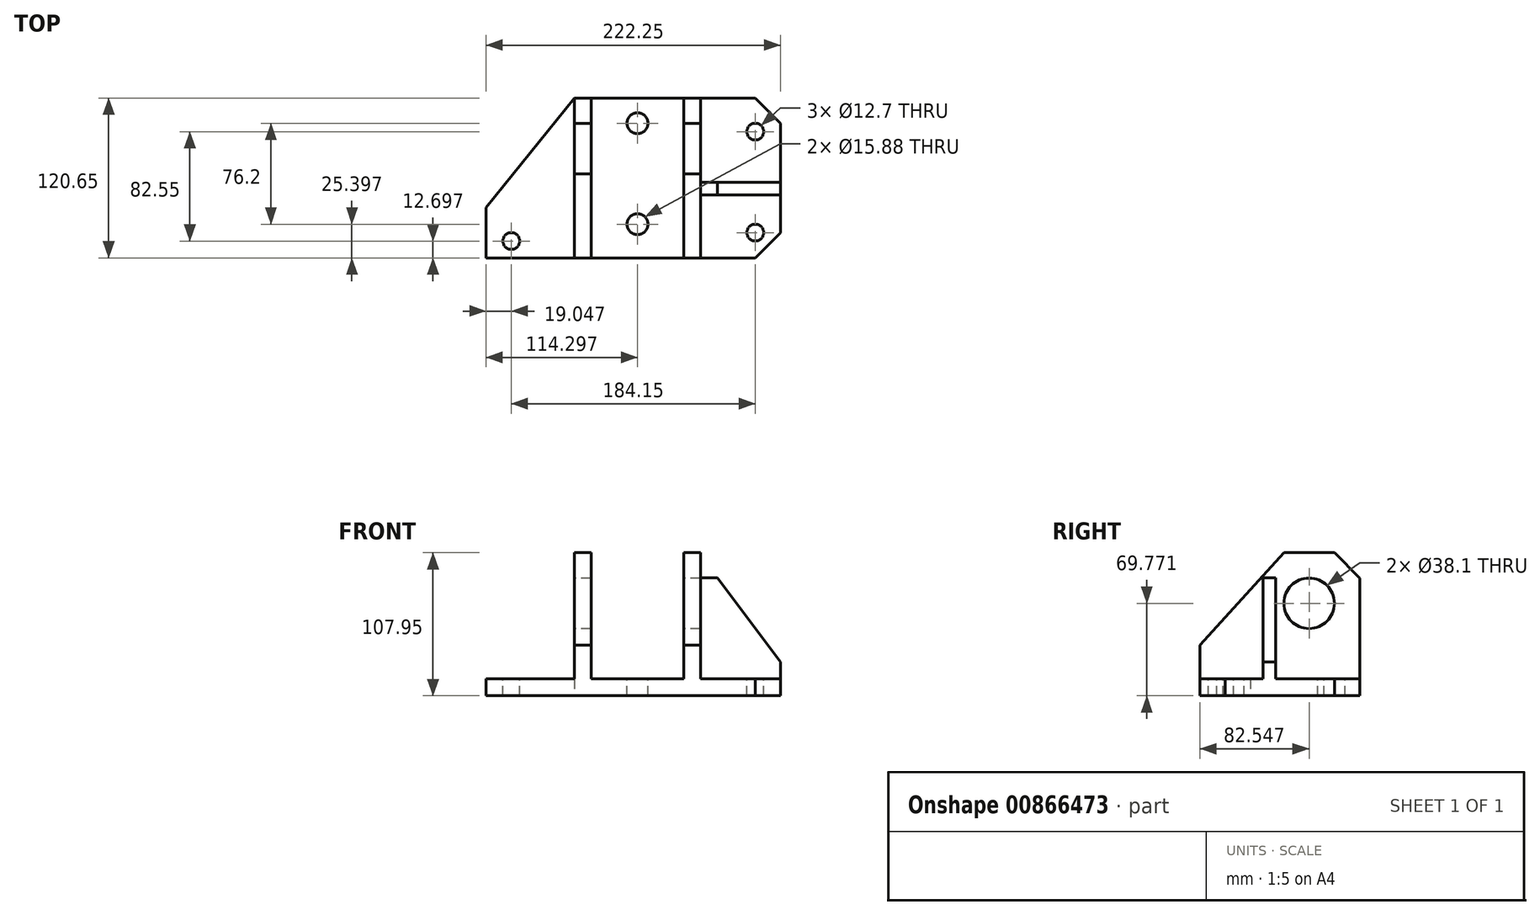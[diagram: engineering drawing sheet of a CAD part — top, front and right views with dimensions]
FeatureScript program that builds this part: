
annotation { "Feature Type Name" : "Feature", "Feature Type Description" : "" }
export const myFeature = defineFeature(function(context is Context, id is Id, definition is map)
    precondition{}
    {
        {
            var Q0;
            Q0=qCreatedBy(makeId("Top.planeOp"),FACE);
            var sketch = newSketch(context, id + "F0", { "sketchPlane" : qUnion([Q0])});
            skLineSegment(sketch, "E0", {"start": v(-97.7, 21.46) * mm, "end": v(-97.7, -16.64) * mm});
            skLineSegment(sketch, "E1", {"start": v(-97.7, -16.64) * mm, "end": v(105.5, -16.64) * mm});
            skLineSegment(sketch, "E2", {"start": v(105.5, -16.64) * mm, "end": v(124.56, 2.4) * mm});
            skLineSegment(sketch, "E3", {"start": v(124.56, 2.4) * mm, "end": v(124.56, 84.96) * mm});
            skLineSegment(sketch, "E4", {"start": v(124.56, 84.96) * mm, "end": v(105.5, 104) * mm});
            skLineSegment(sketch, "E5", {"start": v(105.5, 104) * mm, "end": v(-31.02, 104) * mm});
            skLineSegment(sketch, "E6", {"start": v(-31.02, 104) * mm, "end": v(-97.7, 21.46) * mm});
            skSolve(sketch);
        }
        {
            var Q0;
            Q0=makeQuery(id+"F0.imprint","IMPRINT",FACE,{"disambiguationData":[TD([[makeQuery(id+"F0.imprint","IMPRINT",EDGE,{"derivedFrom":sQuery(id+"F0.wireOp",EDGE,"E0")}),1.0]])]});
            extrude(context, id + "F1", {"entities" : qUnion([Q0]), "depth" : 12.7 * mm, "offsetDistance" : 25.4 * mm});
        }
        {
            var Q0;
            Q0=makeQuery(id+"F1.opExtrude","CAP_FACE",FACE,{"disambiguationData":[OSD([sQuery(id+"F0.wireOp",EDGE,"E0"),sQuery(id+"F0.wireOp",EDGE,"E1"),sQuery(id+"F0.wireOp",EDGE,"E2"),sQuery(id+"F0.wireOp",EDGE,"E3"),sQuery(id+"F0.wireOp",EDGE,"E4"),sQuery(id+"F0.wireOp",EDGE,"E5"),sQuery(id+"F0.wireOp",EDGE,"E6")])],"isStart":false});
            var sketch = newSketch(context, id + "F2", { "sketchPlane" : qUnion([Q0])});
            skLineSegment(sketch, "E7", {"start": v(-31.02, 104) * mm, "end": v(-31.02, -16.64) * mm});
            skLineSegment(sketch, "E8", {"start": v(-18.32, 104) * mm, "end": v(-18.32, -16.64) * mm});
            skLineSegment(sketch, "E9", {"start": v(51.53, -16.64) * mm, "end": v(51.53, 104) * mm});
            skLineSegment(sketch, "E10", {"start": v(64.23, 104) * mm, "end": v(64.23, -16.64) * mm});
            skLineSegment(sketch, "E11", {"start": v(51.53, 104) * mm, "end": v(-18.32, 104) * mm});
            skLineSegment(sketch, "E12", {"start": v(16.6, 104) * mm, "end": v(16.6, -16.64) * mm, "construction": true});
            skCircle(sketch, "E13", {"center": v(-78.64, -3.94) * mm, "radius": 6.35 * mm});
            skCircle(sketch, "E14", {"center": v(16.6, 8.76) * mm, "radius": 7.94 * mm});
            skCircle(sketch, "E15", {"center": v(16.6, 84.96) * mm, "radius": 7.94 * mm});
            skCircle(sketch, "E16", {"center": v(105.5, 2.4) * mm, "radius": 6.35 * mm});
            skCircle(sketch, "E17", {"center": v(105.5, 78.6) * mm, "radius": 6.35 * mm});
            skLineSegment(sketch, "E18", {"start": v(64.23, 30.98) * mm, "end": v(124.56, 30.98) * mm});
            skLineSegment(sketch, "E19", {"start": v(64.23, 40.5) * mm, "end": v(124.56, 40.5) * mm});
            skSolve(sketch);
        }
        {
            var Q0;
            Q0=makeQuery(id+"F2.imprint","IMPRINT",FACE,{"disambiguationData":[TD([[makeQuery(id+"F2.imprint","IMPRINT",EDGE,{"derivedFrom":sQuery(id+"F2.wireOp",EDGE,"E13")}),1.0]])]});
            var Q1;
            Q1=makeQuery(id+"F2.imprint","IMPRINT",FACE,{"disambiguationData":[TD([[makeQuery(id+"F2.imprint","IMPRINT",EDGE,{"derivedFrom":sQuery(id+"F2.wireOp",EDGE,"E14")}),1.0]])]});
            var Q2;
            Q2=makeQuery(id+"F2.imprint","IMPRINT",FACE,{"disambiguationData":[TD([[makeQuery(id+"F2.imprint","IMPRINT",EDGE,{"derivedFrom":sQuery(id+"F2.wireOp",EDGE,"E15")}),1.0]])]});
            var Q3;
            Q3=makeQuery(id+"F2.imprint","IMPRINT",FACE,{"disambiguationData":[TD([[makeQuery(id+"F2.imprint","IMPRINT",EDGE,{"derivedFrom":sQuery(id+"F2.wireOp",EDGE,"E16")}),1.0]])]});
            var Q4;
            Q4=makeQuery(id+"F2.imprint","IMPRINT",FACE,{"disambiguationData":[TD([[makeQuery(id+"F2.imprint","IMPRINT",EDGE,{"derivedFrom":sQuery(id+"F2.wireOp",EDGE,"E17")}),1.0]])]});
            extrude(context, id + "F3", {"entities" : qUnion([Q0, Q1, Q2, Q3, Q4]), "operationType" : NewBodyOperationType.REMOVE, "endBound" : BoundingType.THROUGH_ALL, "oppositeDirection" : true, "depth" : 25.4 * mm, "offsetDistance" : 25.4 * mm});
        }
        {
            var Q0;
            {var subQ0=sQuery(id+"F2.wireOp",EDGE,"E18");Q0=makeQuery(id+"F2.imprint","IMPRINT",FACE,{"disambiguationData":[TD([[makeQuery(id+"F2.imprint","IMPRINT",EDGE,{"derivedFrom":subQ0}),1.0]])]});}
            extrude(context, id + "F4", {"entities" : qUnion([Q0]), "operationType" : NewBodyOperationType.ADD, "depth" : 76.2 * mm, "offsetDistance" : 25.4 * mm});
        }
        {
            var Q0;
            {var subQ7=sQuery(id+"F2.wireOp",EDGE,"E9");Q0=makeQuery(id+"F2.imprint","IMPRINT",FACE,{"disambiguationData":[TD([[makeQuery(id+"F2.imprint","IMPRINT",EDGE,{"derivedFrom":subQ7}),-1.0]])]});}
            var Q1;
            {var subQ0=sQuery(id+"F2.wireOp",EDGE,"E7");Q1=makeQuery(id+"F2.imprint","IMPRINT",FACE,{"disambiguationData":[TD([[makeQuery(id+"F2.imprint","IMPRINT",EDGE,{"derivedFrom":subQ0}),1.0]])]});}
            extrude(context, id + "F5", {"entities" : qUnion([Q0, Q1]), "operationType" : NewBodyOperationType.ADD, "depth" : 95.25 * mm, "offsetDistance" : 25.4 * mm});
        }
        {
            var Q0;
            Q0=makeQuery(id+"F4.opExtrude","SWEPT_FACE",FACE,{"disambiguationData":[OSD([sQuery(id+"F2.wireOp",EDGE,"E18")])]});
            var sketch = newSketch(context, id + "F6", { "sketchPlane" : qUnion([Q0])});
            skLineSegment(sketch, "E20", {"start": v(76.93, 88.9) * mm, "end": v(124.56, 25.4) * mm});
            skSolve(sketch);
        }
        {
            var Q0;
            Q0 = qSketchRegion(id + "F6", true);
            var Q1;
            {var subQ0=sQuery(id+"F6.wireOp",EDGE,"E20");Q1=makeQuery(id+"F6.imprint","IMPRINT",FACE,{"disambiguationData":[TD([[makeQuery(id+"F6.imprint","IMPRINT",EDGE,{"derivedFrom":subQ0}),1.0]])]});}
            extrude(context, id + "F7", {"entities" : qUnion([Q0, Q1]), "operationType" : NewBodyOperationType.REMOVE, "endBound" : BoundingType.THROUGH_ALL, "oppositeDirection" : true, "depth" : 25.4 * mm, "offsetDistance" : 25.4 * mm});
        }
        {
            var Q0;
            Q0=makeQuery(id+"F5.opExtrude","SWEPT_FACE",FACE,{"disambiguationData":[OSD([sQuery(id+"F2.wireOp",EDGE,"E7")])]});
            var sketch = newSketch(context, id + "F8", { "sketchPlane" : qUnion([Q0])});
            skLineSegment(sketch, "E21", {"start": v(-104, 88.82) * mm, "end": v(-84.96, 107.95) * mm});
            skLineSegment(sketch, "E22", {"start": v(-84.96, 107.95) * mm, "end": v(-46.86, 107.95) * mm});
            skLineSegment(sketch, "E23", {"start": v(-46.86, 107.95) * mm, "end": v(16.64, 38.1) * mm});
            skCircle(sketch, "E24", {"center": v(-65.9, 69.77) * mm, "radius": 19.05 * mm});
            skSolve(sketch);
        }
        {
            var Q0;
            {var subQ0=sQuery(id+"F8.wireOp",EDGE,"E23");Q0=makeQuery(id+"F8.imprint","IMPRINT",FACE,{"disambiguationData":[TD([[makeQuery(id+"F8.imprint","IMPRINT",EDGE,{"derivedFrom":subQ0}),1.0]])]});}
            var Q1;
            {var subQ0=sQuery(id+"F8.wireOp",EDGE,"E21");Q1=makeQuery(id+"F8.imprint","IMPRINT",FACE,{"disambiguationData":[TD([[makeQuery(id+"F8.imprint","IMPRINT",EDGE,{"derivedFrom":subQ0}),1.0]])]});}
            var Q2;
            Q2=makeQuery(id+"F8.imprint","IMPRINT",FACE,{"disambiguationData":[TD([[makeQuery(id+"F8.imprint","IMPRINT",EDGE,{"derivedFrom":sQuery(id+"F8.wireOp",EDGE,"E24")}),1.0]])]});
            extrude(context, id + "F9", {"entities" : qUnion([Q0, Q1, Q2]), "operationType" : NewBodyOperationType.REMOVE, "endBound" : BoundingType.THROUGH_ALL, "oppositeDirection" : true, "depth" : 25.4 * mm, "offsetDistance" : 25.4 * mm});
        }
    });
